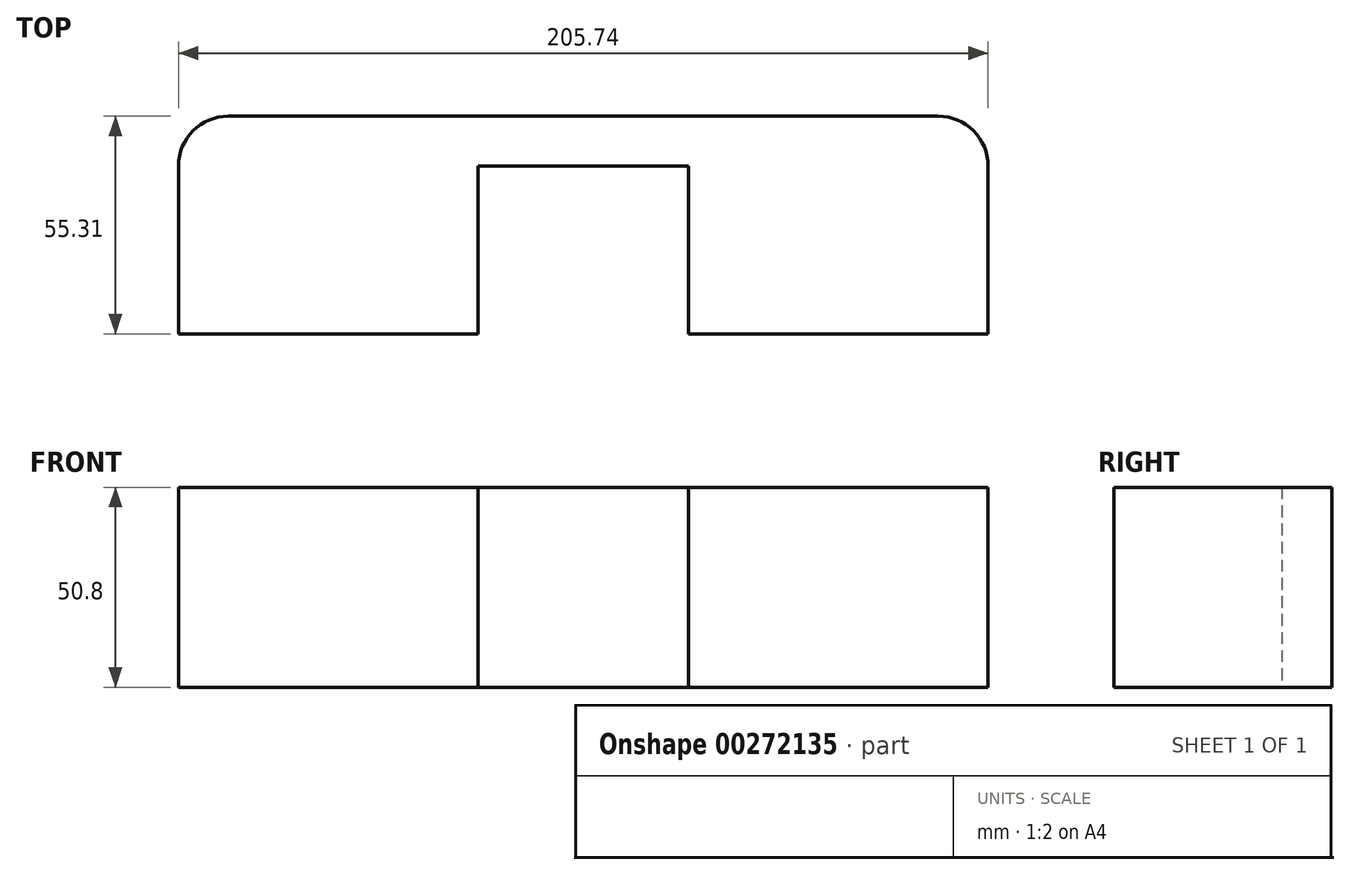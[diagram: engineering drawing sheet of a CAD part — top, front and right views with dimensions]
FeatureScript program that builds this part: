
annotation { "Feature Type Name" : "Feature", "Feature Type Description" : "" }
export const myFeature = defineFeature(function(context is Context, id is Id, definition is map)
    precondition{}
    {
        {
            var Q0;
            Q0=qCreatedBy(makeId("Top.planeOp"),FACE);
            var sketch = newSketch(context, id + "F0", { "sketchPlane" : qUnion([Q0])});
            skLineSegment(sketch, "E0.bottom", {"start": v(-102.87, -1.57) * mm, "end": v(-26.67, -1.57) * mm});
            skLineSegment(sketch, "E0.top", {"start": v(-102.87, -26.97) * mm, "end": v(-26.67, -26.97) * mm});
            skLineSegment(sketch, "E0.left", {"start": v(-102.87, -1.57) * mm, "end": v(-102.87, -26.97) * mm});
            skLineSegment(sketch, "E0.right", {"start": v(-26.67, -1.57) * mm, "end": v(-26.67, -26.97) * mm});
            skLineSegment(sketch, "E1.top", {"start": v(-90.17, 28.34) * mm, "end": v(-26.67, 28.34) * mm});
            skLineSegment(sketch, "E1.left", {"start": v(-102.87, -1.57) * mm, "end": v(-102.87, 15.64) * mm});
            skLineSegment(sketch, "E1.right", {"start": v(-26.67, -1.57) * mm, "end": v(-26.67, 28.34) * mm});
            skPoint(sketch, "E2.visualSharp", {"position": v(-102.87, 28.34) * mm});
            skArc(sketch, "E2.filletArc", {"start": v(-90.17, 28.34) * mm, "mid": v(-99.15, 24.62) * mm, "end": v(-102.87, 15.64) * mm});
            skLineSegment(sketch, "E3.bottom", {"start": v(-90.17, 28.34) * mm, "end": v(90.17, 28.34) * mm});
            skLineSegment(sketch, "E3.top", {"start": v(-90.17, 15.64) * mm, "end": v(90.17, 15.64) * mm});
            skLineSegment(sketch, "E3.left", {"start": v(-90.17, 28.34) * mm, "end": v(-90.17, 15.64) * mm});
            skLineSegment(sketch, "E3.right", {"start": v(90.17, 28.34) * mm, "end": v(90.17, 15.64) * mm});
            skLineSegment(sketch, "E4.MirrorCS", {"start": v(26.67, -1.57) * mm, "end": v(26.67, 28.34) * mm});
            skLineSegment(sketch, "E5.MirrorCS", {"start": v(102.87, -1.57) * mm, "end": v(102.87, 15.64) * mm});
            skArc(sketch, "E6.MirrorCS", {"start": v(90.17, 28.34) * mm, "mid": v(99.15, 24.62) * mm, "end": v(102.87, 15.64) * mm});
            skLineSegment(sketch, "E7.MirrorCS", {"start": v(102.87, -1.57) * mm, "end": v(26.67, -1.57) * mm});
            skLineSegment(sketch, "E8.MirrorCS", {"start": v(102.87, -1.57) * mm, "end": v(102.87, -26.97) * mm});
            skLineSegment(sketch, "E9.MirrorCS", {"start": v(102.87, -26.97) * mm, "end": v(26.67, -26.97) * mm});
            skLineSegment(sketch, "E10.MirrorCS", {"start": v(26.67, -1.57) * mm, "end": v(26.67, -26.97) * mm});
            skSolve(sketch);
        }
        {
            var Q0;
            {var subQ5=sQuery(id+"F0.wireOp",EDGE,"E3.left");Q0=makeQuery(id+"F0.imprint","IMPRINT",FACE,{"disambiguationData":[TD([[makeQuery(id+"F0.imprint","IMPRINT",EDGE,{"derivedFrom":subQ5}),1.0]])]});}
            var Q1;
            {var subQ2=sQuery(id+"F0.wireOp",EDGE,"E0.bottom");Q1=makeQuery(id+"F0.imprint","IMPRINT",FACE,{"disambiguationData":[TD([[makeQuery(id+"F0.imprint","IMPRINT",EDGE,{"derivedFrom":subQ2}),1.0]])]});}
            var Q2;
            Q2=makeQuery(id+"F0.imprint","IMPRINT",FACE,{"disambiguationData":[TD([[makeQuery(id+"F0.imprint","IMPRINT",EDGE,{"derivedFrom":sQuery(id+"F0.wireOp",EDGE,"E0.top")}),1.0]])]});
            var Q3;
            {var subQ0=sQuery(id+"F0.wireOp",EDGE,"E3.bottom");var subQ1=sQuery(id+"F0.wireOp",EDGE,"E1.right");var subQ2=makeQuery(id+"F0.imprint","INTERSECT",VERTEX,{"derivedFrom":[subQ1,subQ0]});Q3=makeQuery(id+"F0.imprint","IMPRINT",FACE,{"disambiguationData":[TD([[makeQuery(id+"F0.imprint","IMPRINT",EDGE,{"disambiguationData":[TD([[subQ2,1.0]])],"derivedFrom":subQ1}),-1.0]])]});}
            var Q4;
            {var subQ0=sQuery(id+"F0.wireOp",EDGE,"E3.right");Q4=makeQuery(id+"F0.imprint","IMPRINT",FACE,{"disambiguationData":[TD([[makeQuery(id+"F0.imprint","IMPRINT",EDGE,{"derivedFrom":subQ0}),-1.0]])]});}
            var Q5;
            {var subQ4=sQuery(id+"F0.wireOp",EDGE,"E3.right");Q5=makeQuery(id+"F0.imprint","IMPRINT",FACE,{"disambiguationData":[TD([[makeQuery(id+"F0.imprint","IMPRINT",EDGE,{"derivedFrom":subQ4}),1.0]])]});}
            var Q6;
            Q6=makeQuery(id+"F0.imprint","IMPRINT",FACE,{"disambiguationData":[TD([[makeQuery(id+"F0.imprint","IMPRINT",EDGE,{"derivedFrom":sQuery(id+"F0.wireOp",EDGE,"E7.MirrorCS")}),1.0]])]});
            extrude(context, id + "F1", {"entities" : qUnion([Q0, Q1, Q2, Q3, Q4, Q5, Q6]), "depth" : 50.8 * mm});
        }
    });
